# Revit family: Gitterrinne GRM - GRM 55 400 G
name_source: partatom
category: Generic Models
revit_build: Autodesk Revit 2017 (Build: 20190508_0315(x64)
units: mm (PartAtom-declared; Revit-internal decimal feet)

## family parameters
Always vertical = Yes
Can host rebar = No
Cut with Voids When Loaded = No
Part Type = Normal
Room Calculation Point = No
Round Connector Dimension = Use Diameter
Shared = No
Work Plane-Based = No

## types (4) — shared parameters
Length = 3000 mm  [stored 9.84252 ft]
Manufacturer = OBO Bettermann
URL = http://www.obo-bettermann.com
Width = 400 mm  [stored 1.31234 ft]
Width 1 = 200 mm  [stored 0.656168 ft]

## per-type parameters (varying)
| type | GTIN | Manufacturer Art.No. | Material |
| GRM 55 400 G | 4012196858736 | 6001450 | Electrogalvanised |
| GRM 55 400 FT | 4012196815111 | 6001428 | Hot-dip galvanised |
| GRM 55 400 A2 | 4012196102198 | 6001080 | Stainless steel, A2 |
| GRM 55 400 A4 | 4012195166085 | 6001095 | Stainless steel, A4 |

note: column(s) folded — value = type name in every type: Article Type

note: [stored X ft] marks values corroborated as IEEE doubles in the binary element streams (Revit-internal decimal feet)

## geometry (parser evidence)
native form markers: Sweep x2
no freeform markers — native parametric forms only
